# Revit family: Rollenlager , axial M10 bis dreiviertel Zoll
name_source: partatom
category: HLS-Bauteile
revit_build: Autodesk Revit 2017 (Build: 20190507_1515(x64)
units: mm (PartAtom-declared; Revit-internal decimal feet)

## family parameters
Basisbauteil = Fläche
Beim Laden mit Abzugskörper schneiden = Nein
Bemaßung runder Anschluss = Durchmesser verwenden
Gemeinsam genutzt = Ja
Raumberechnungspunkt = Nein
Teiletyp = Normal

## types (5) — shared parameters
Breite = 120 mm  [stored 0.393701 ft]
Fabrikat = MEFA
Firma = MEFA Befestigungs- und Montagesysteme GmbH
Kurztext1 = Rollenlager axial
Langloch = 13 x 20 mm
Lochabstand = 100 mm
Länge = 190 mm
Material = Stahl
Materialname = S235
Mengeneinheit = St
Oberflaeche = galvanisch verzinkt
Rollwiderstand = 0,004 - 0,02
Vorgabe-Ansicht = 1219 mm
max. Schiebeweg axial = 120 mm
max. Temperaturbeständigkeit = 300 °C
max. zul. Last Druck = 0.90 kip
max. zul. Last Zug = 0.90 kip
vpe = 1 St

## per-type parameters (varying)
| type | Anschluss | Artikelnummer | Bauhöhe | EAN | Gewicht | Gewicht pro Bauteil | Kurztext2 | Typ |
| Rollenlager, axial M16 | M16 | 175811816 | 65 mm | 4250928437389 | 1.97 kg | 1.97 kg | Anschluss M16 | Rollenlager , axial M16 |
| Rollenlager, axial M12 | M12 | 175811813 | 65 mm | 4250928448804 | 1.91 kg | 1.91 kg | Anschluss M12 | Rollenlager , axial M12 |
| Rollenlager, axial M10 | M10 | 175811811 | 65 mm | 4250928448798 | 1.93 kg | 1.93 kg | Anschluss M10 | Rollenlager , axial M10 |
| Rollenlager, axial 1/2" | 1/2'' | 175811839 | 45 mm | 4250928437396 | 1.92 kg | 1.92 kg | Anschluss 1/2'' | Rollenlager , axial Halbzoll |
| Rollenlager, axial 3/4" | 3/4'' | 175811840 | 86 mm | 4250928437402 | 2.09 kg | 2.09 kg | Anschluss 3/4'' | Rollenlager , axial dreiviertelzoll |

note: [stored X ft] marks values corroborated as IEEE doubles in the binary element streams (Revit-internal decimal feet)
